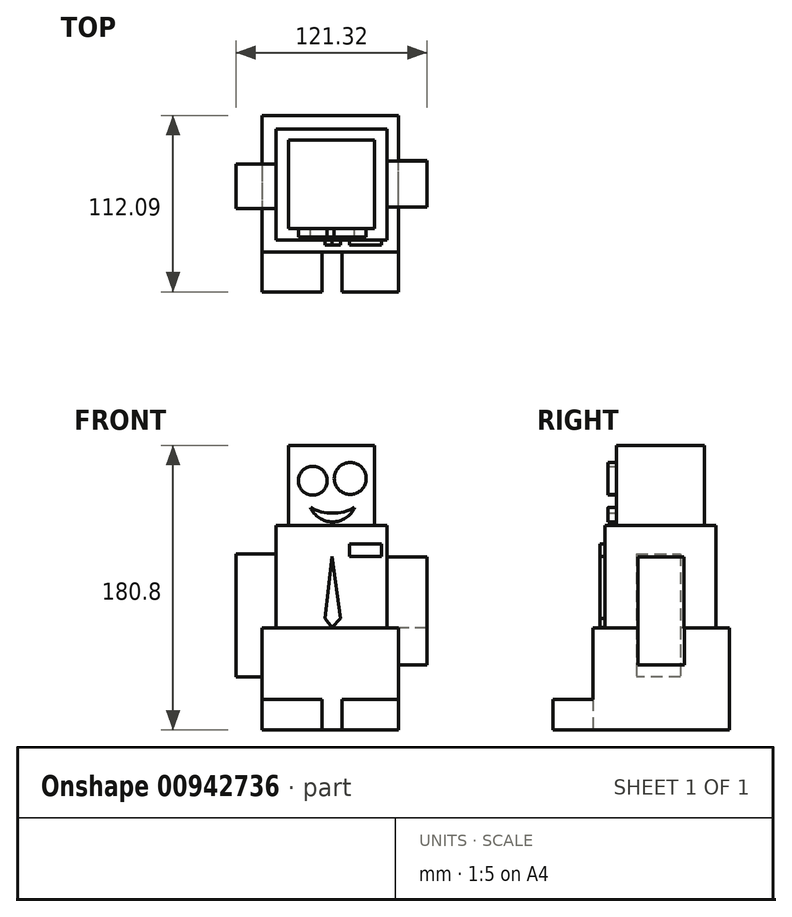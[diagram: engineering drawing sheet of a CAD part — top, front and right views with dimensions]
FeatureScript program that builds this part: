
annotation { "Feature Type Name" : "Feature", "Feature Type Description" : "" }
export const myFeature = defineFeature(function(context is Context, id is Id, definition is map)
    precondition{}
    {
        {
            var Q0;
            Q0=qCreatedBy(makeId("Top.planeOp"),FACE);
            var sketch = newSketch(context, id + "F0", { "sketchPlane" : qUnion([Q0])});
            skLineSegment(sketch, "E0", {"start": v(42.5, 48.7) * mm, "end": v(-44.2, 48.7) * mm});
            skLineSegment(sketch, "E1", {"start": v(-44.2, 48.7) * mm, "end": v(-44.2, -38) * mm});
            skLineSegment(sketch, "E2", {"start": v(-44.2, -38) * mm, "end": v(42.5, -38) * mm});
            skLineSegment(sketch, "E3", {"start": v(42.5, -38) * mm, "end": v(42.5, 48.7) * mm});
            skSolve(sketch);
        }
        {
            var Q0;
            Q0 = qSketchRegion(id + "F0", true);
            extrude(context, id + "F1", {"entities" : qUnion([Q0]), "depth" : 65 * mm, "offsetDistance" : 25.4 * mm});
        }
        {
            var Q0;
            Q0=makeQuery(id+"F1.opExtrude","CAP_FACE",FACE,{"disambiguationData":[OSD([sQuery(id+"F0.wireOp",EDGE,"E0"),sQuery(id+"F0.wireOp",EDGE,"E1"),sQuery(id+"F0.wireOp",EDGE,"E2"),sQuery(id+"F0.wireOp",EDGE,"E3")])],"isStart":false});
            var sketch = newSketch(context, id + "F2", { "sketchPlane" : qUnion([Q0])});
            skLineSegment(sketch, "E4.bottom", {"start": v(-35.26, 40.15) * mm, "end": v(35.26, 40.15) * mm});
            skLineSegment(sketch, "E4.top", {"start": v(-35.26, -30.36) * mm, "end": v(35.26, -30.36) * mm});
            skLineSegment(sketch, "E4.left", {"start": v(-35.26, 40.15) * mm, "end": v(-35.26, -30.36) * mm});
            skLineSegment(sketch, "E4.right", {"start": v(35.26, 40.15) * mm, "end": v(35.26, -30.36) * mm});
            skSolve(sketch);
        }
        {
            var Q0;
            Q0 = qSketchRegion(id + "F2", true);
            extrude(context, id + "F3", {"entities" : qUnion([Q0]), "operationType" : NewBodyOperationType.ADD, "depth" : 65 * mm, "offsetDistance" : 25.4 * mm});
        }
        {
            var Q0;
            Q0=makeQuery(id+"F3.opExtrude","CAP_FACE",FACE,{"disambiguationData":[OSD([sQuery(id+"F2.wireOp",EDGE,"E4.bottom"),sQuery(id+"F2.wireOp",EDGE,"E4.top"),sQuery(id+"F2.wireOp",EDGE,"E4.left"),sQuery(id+"F2.wireOp",EDGE,"E4.right")])],"isStart":false});
            var sketch = newSketch(context, id + "F4", { "sketchPlane" : qUnion([Q0])});
            skLineSegment(sketch, "E5.bottom", {"start": v(-27.2, 32.95) * mm, "end": v(27.2, 32.95) * mm});
            skLineSegment(sketch, "E5.top", {"start": v(-27.2, -23.17) * mm, "end": v(27.2, -23.17) * mm});
            skLineSegment(sketch, "E5.left", {"start": v(-27.2, 32.95) * mm, "end": v(-27.2, -23.17) * mm});
            skLineSegment(sketch, "E5.right", {"start": v(27.2, 32.95) * mm, "end": v(27.2, -23.17) * mm});
            skPoint(sketch, "E5.middle", {"position": v(0, 4.9) * mm});
            skPoint(sketch, "E5.middle.positionSnap0", {"position": v(0, 40.15) * mm});
            skPoint(sketch, "E5.middle.positionSnap1", {"position": v(-35.26, 4.9) * mm});
            skPoint(sketch, "E5.centerSnap0", {"position": v(0, 40.15) * mm});
            skPoint(sketch, "E5.centerSnap1", {"position": v(-35.26, 4.9) * mm});
            skSolve(sketch);
        }
        {
            var Q0;
            Q0=makeQuery(id+"F4.imprint","IMPRINT",FACE,{"disambiguationData":[TD([[makeQuery(id+"F4.imprint","IMPRINT",EDGE,{"derivedFrom":sQuery(id+"F4.wireOp",EDGE,"E5.bottom")}),-1.0]])]});
            extrude(context, id + "F5", {"entities" : qUnion([Q0]), "operationType" : NewBodyOperationType.ADD, "depth" : 50.8 * mm, "offsetDistance" : 25.4 * mm});
        }
        {
            var Q0;
            Q0=makeQuery(id+"F5.opExtrude","SWEPT_FACE",FACE,{"disambiguationData":[OSD([sQuery(id+"F4.wireOp",EDGE,"E5.top")])]});
            var sketch = newSketch(context, id + "F6", { "sketchPlane" : qUnion([Q0])});
            skCircle(sketch, "E6", {"center": v(-11.9, 158.34) * mm, "radius": 9.12 * mm});
            skCircle(sketch, "E7", {"center": v(11.9, 159.8) * mm, "radius": 10.15 * mm});
            skArc(sketch, "E8", {"start": v(-15.29, 137.48) * mm, "mid": v(0.8, 132.86) * mm, "end": v(16.74, 137.96) * mm});
            skLineSegment(sketch, "E9", {"start": v(0.24, 110.3) * mm, "end": v(0.24, 65.16) * mm});
            skLineSegment(sketch, "E10", {"start": v(0.24, 110.3) * mm, "end": v(-4.13, 70.98) * mm});
            skLineSegment(sketch, "E11", {"start": v(-4.13, 70.98) * mm, "end": v(0.24, 65.16) * mm});
            skLineSegment(sketch, "E12", {"start": v(5.58, 70.98) * mm, "end": v(0.24, 110.3) * mm});
            skLineSegment(sketch, "E13", {"start": v(5.58, 70.98) * mm, "end": v(0.24, 65.16) * mm});
            skLineSegment(sketch, "E14.bottom", {"start": v(11.4, 118.06) * mm, "end": v(31.79, 118.06) * mm});
            skLineSegment(sketch, "E14.top", {"start": v(11.4, 110.3) * mm, "end": v(31.79, 110.3) * mm});
            skLineSegment(sketch, "E14.left", {"start": v(11.4, 118.06) * mm, "end": v(11.4, 110.3) * mm});
            skLineSegment(sketch, "E14.right", {"start": v(31.79, 118.06) * mm, "end": v(31.79, 110.3) * mm});
            skLineSegment(sketch, "E15", {"start": v(0.24, 57.88) * mm, "end": v(0.24, 0.61) * mm});
            skSolve(sketch);
        }
        {
            var Q0;
            Q0 = qSketchRegion(id + "F6", true);
            extrude(context, id + "F7", {"entities" : qUnion([Q0]), "operationType" : NewBodyOperationType.ADD, "depth" : 25.4 * mm, "offsetDistance" : 25.4 * mm});
        }
        {
            var Q0;
            Q0=makeQuery(id+"F3.opExtrude","SWEPT_FACE",FACE,{"disambiguationData":[OSD([sQuery(id+"F2.wireOp",EDGE,"E4.right")])]});
            var sketch = newSketch(context, id + "F8", { "sketchPlane" : qUnion([Q0])});
            skLineSegment(sketch, "E16.bottom", {"start": v(-9.46, 109.81) * mm, "end": v(19.66, 109.81) * mm});
            skLineSegment(sketch, "E16.top", {"start": v(-9.46, 65) * mm, "end": v(19.66, 65) * mm});
            skLineSegment(sketch, "E16.left", {"start": v(-9.46, 109.81) * mm, "end": v(-9.46, 65) * mm});
            skLineSegment(sketch, "E16.right", {"start": v(19.66, 109.81) * mm, "end": v(19.66, 65) * mm});
            skSolve(sketch);
        }
        {
            var Q0;
            Q0 = qSketchRegion(id + "F8", true);
            extrude(context, id + "F9", {"entities" : qUnion([Q0]), "operationType" : NewBodyOperationType.ADD, "depth" : 25.4 * mm, "offsetDistance" : 25.4 * mm});
        }
        {
            var Q0;
            Q0=makeQuery(id+"F3.opExtrude","SWEPT_FACE",FACE,{"disambiguationData":[OSD([sQuery(id+"F2.wireOp",EDGE,"E4.right")])]});
            var sketch = newSketch(context, id + "F10", { "sketchPlane" : qUnion([Q0])});
            skLineSegment(sketch, "E17.bottom", {"start": v(-9.46, 65) * mm, "end": v(20.1, 65) * mm});
            skLineSegment(sketch, "E17.top", {"start": v(-9.46, 41.38) * mm, "end": v(20.1, 41.38) * mm});
            skLineSegment(sketch, "E17.left", {"start": v(-9.46, 65) * mm, "end": v(-9.46, 41.38) * mm});
            skLineSegment(sketch, "E17.right", {"start": v(20.1, 65) * mm, "end": v(20.1, 41.38) * mm});
            skSolve(sketch);
        }
        {
            var Q0;
            Q0 = qSketchRegion(id + "F10", true);
            extrude(context, id + "F11", {"entities" : qUnion([Q0]), "operationType" : NewBodyOperationType.ADD, "depth" : 25.4 * mm, "offsetDistance" : 25.4 * mm});
        }
        {
            var Q0;
            Q0=makeQuery(id+"F3.opExtrude","SWEPT_FACE",FACE,{"disambiguationData":[OSD([sQuery(id+"F2.wireOp",EDGE,"E4.left")])]});
            var sketch = newSketch(context, id + "F12", { "sketchPlane" : qUnion([Q0])});
            skLineSegment(sketch, "E18.bottom", {"start": v(10.43, 111.75) * mm, "end": v(-17.71, 111.75) * mm});
            skLineSegment(sketch, "E18.top", {"start": v(10.43, 65) * mm, "end": v(-17.71, 65) * mm});
            skLineSegment(sketch, "E18.left", {"start": v(10.43, 111.75) * mm, "end": v(10.43, 65) * mm});
            skLineSegment(sketch, "E18.right", {"start": v(-17.71, 111.75) * mm, "end": v(-17.71, 65) * mm});
            skLineSegment(sketch, "E19.bottom", {"start": v(-17.71, 65) * mm, "end": v(10.43, 65) * mm});
            skLineSegment(sketch, "E19.top", {"start": v(-17.71, 33.61) * mm, "end": v(10.43, 33.61) * mm});
            skLineSegment(sketch, "E19.left", {"start": v(-17.71, 65) * mm, "end": v(-17.71, 33.61) * mm});
            skLineSegment(sketch, "E19.right", {"start": v(10.43, 65) * mm, "end": v(10.43, 33.61) * mm});
            skSolve(sketch);
        }
        {
            var Q0;
            Q0 = qSketchRegion(id + "F12", true);
            extrude(context, id + "F13", {"entities" : qUnion([Q0]), "operationType" : NewBodyOperationType.ADD, "depth" : 25.4 * mm, "offsetDistance" : 25.4 * mm});
        }
        {
            var Q0;
            Q0=makeQuery(id+"F5.opExtrude","SWEPT_FACE",FACE,{"disambiguationData":[OSD([sQuery(id+"F4.wireOp",EDGE,"E5.top")])]});
            var sketch = newSketch(context, id + "F14", { "sketchPlane" : qUnion([Q0])});
            skArc(sketch, "E20", {"start": v(-13.4, 141.36) * mm, "mid": v(0.66, 132.24) * mm, "end": v(14.74, 141.32) * mm});
            skArc(sketch, "E21", {"start": v(-13.4, 141.36) * mm, "mid": v(0.67, 137.76) * mm, "end": v(14.74, 141.32) * mm});
            skSolve(sketch);
        }
        {
            var Q0;
            Q0 = qSketchRegion(id + "F14", true);
            extrude(context, id + "F15", {"entities" : qUnion([Q0]), "operationType" : NewBodyOperationType.ADD, "depth" : 25.4 * mm, "offsetDistance" : 25.4 * mm});
        }
        {
            var Q0;
            Q0=makeQuery(id+"F1.opExtrude","SWEPT_FACE",FACE,{"disambiguationData":[OSD([sQuery(id+"F0.wireOp",EDGE,"E2")])]});
            var sketch = newSketch(context, id + "F16", { "sketchPlane" : qUnion([Q0])});
            skLineSegment(sketch, "E22.bottom", {"start": v(-6.07, 19.54) * mm, "end": v(-44.2, 19.54) * mm});
            skLineSegment(sketch, "E22.top", {"start": v(-6.07, 0) * mm, "end": v(-44.2, 0) * mm});
            skLineSegment(sketch, "E22.left", {"start": v(-6.07, 19.54) * mm, "end": v(-6.07, 0) * mm});
            skLineSegment(sketch, "E22.right", {"start": v(-44.2, 19.54) * mm, "end": v(-44.2, 0) * mm});
            skLineSegment(sketch, "E23.bottom", {"start": v(6.55, 19.54) * mm, "end": v(42.5, 19.54) * mm});
            skLineSegment(sketch, "E23.top", {"start": v(6.55, 0) * mm, "end": v(42.5, 0) * mm});
            skLineSegment(sketch, "E23.left", {"start": v(6.55, 19.54) * mm, "end": v(6.55, 0) * mm});
            skLineSegment(sketch, "E23.right", {"start": v(42.5, 19.54) * mm, "end": v(42.5, 0) * mm});
            skSolve(sketch);
        }
        {
            var Q0;
            Q0 = qSketchRegion(id + "F16", true);
            extrude(context, id + "F17", {"entities" : qUnion([Q0]), "operationType" : NewBodyOperationType.ADD, "depth" : 25.4 * mm, "offsetDistance" : 25.4 * mm});
        }
        {
            var Q0;
            Q0=makeQuery(id+"F7.opExtrude","CAP_FACE",FACE,{"disambiguationData":[OSD([sQuery(id+"F6.wireOp",EDGE,"E10"),sQuery(id+"F6.wireOp",EDGE,"E11"),sQuery(id+"F6.wireOp",EDGE,"E12"),sQuery(id+"F6.wireOp",EDGE,"E13")])],"isStart":false});
            var sketch = newSketch(context, id + "F18", { "sketchPlane" : qUnion([Q0])});
            skLineSegment(sketch, "E24.0.0", {"start": v(0.24, 110.3) * mm, "end": v(-4.13, 70.98) * mm});
            skLineSegment(sketch, "E24.0.1", {"start": v(-4.13, 70.98) * mm, "end": v(0.24, 65.16) * mm});
            skLineSegment(sketch, "E24.0.2", {"start": v(0.24, 65.16) * mm, "end": v(5.58, 70.98) * mm});
            skLineSegment(sketch, "E24.0.3", {"start": v(5.58, 70.98) * mm, "end": v(0.24, 110.3) * mm});
            skLineSegment(sketch, "E25.0.0", {"start": v(11.4, 118.06) * mm, "end": v(11.4, 110.3) * mm});
            skLineSegment(sketch, "E25.0.1", {"start": v(11.4, 110.3) * mm, "end": v(31.79, 110.3) * mm});
            skLineSegment(sketch, "E25.0.2", {"start": v(31.79, 110.3) * mm, "end": v(31.79, 118.06) * mm});
            skLineSegment(sketch, "E25.0.3", {"start": v(31.79, 118.06) * mm, "end": v(11.4, 118.06) * mm});
            skSolve(sketch);
        }
        {
            var Q0;
            Q0=makeQuery(id+"F7.opExtrude","CAP_FACE",FACE,{"disambiguationData":[OSD([sQuery(id+"F6.wireOp",EDGE,"E6")])],"isStart":false});
            var Q1;
            Q1=makeQuery(id+"F7.opExtrude","CAP_FACE",FACE,{"disambiguationData":[OSD([sQuery(id+"F6.wireOp",EDGE,"E7")])],"isStart":false});
            var Q2;
            Q2=makeQuery(id+"F15.opExtrude","CAP_FACE",FACE,{"disambiguationData":[OSD([sQuery(id+"F14.wireOp",EDGE,"E20"),sQuery(id+"F14.wireOp",EDGE,"E21")])],"isStart":false});
            extrude(context, id + "F19", {"entities" : qUnion([Q0, Q1, Q2]), "operationType" : NewBodyOperationType.REMOVE, "oppositeDirection" : true, "depth" : 20 * mm, "offsetDistance" : 25.4 * mm});
        }
        {
            var Q0;
            Q0=makeQuery(id+"F18.imprint","IMPRINT",FACE,{"disambiguationData":[TD([[makeQuery(id+"F18.imprint","IMPRINT",EDGE,{"derivedFrom":sQuery(id+"F18.wireOp",EDGE,"E24.0.0")}),1.0]])]});
            var Q1;
            Q1=makeQuery(id+"F18.imprint","IMPRINT",FACE,{"disambiguationData":[TD([[makeQuery(id+"F18.imprint","IMPRINT",EDGE,{"derivedFrom":sQuery(id+"F18.wireOp",EDGE,"E25.0.0")}),1.0]])]});
            extrude(context, id + "F20", {"entities" : qUnion([Q0, Q1]), "operationType" : NewBodyOperationType.REMOVE, "oppositeDirection" : true, "depth" : 15 * mm, "offsetDistance" : 25.4 * mm});
        }
    });
